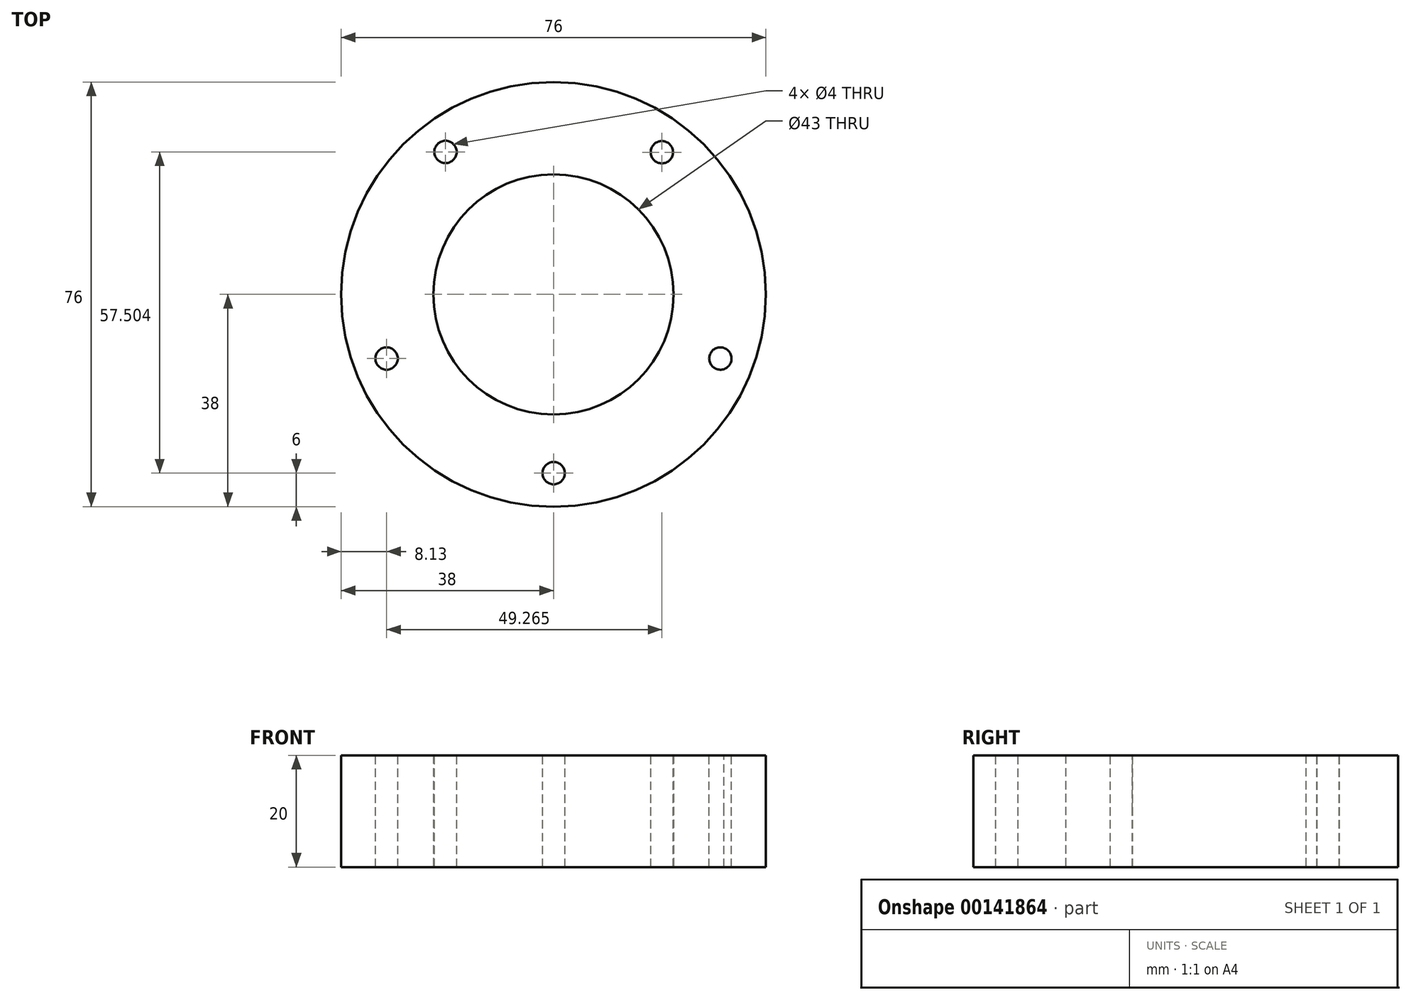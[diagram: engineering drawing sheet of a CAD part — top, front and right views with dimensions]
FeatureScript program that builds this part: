
annotation { "Feature Type Name" : "Feature", "Feature Type Description" : "" }
export const myFeature = defineFeature(function(context is Context, id is Id, definition is map)
    precondition{}
    {
        {
            var Q0;
            Q0=qCreatedBy(makeId("Top.planeOp"),FACE);
            var sketch = newSketch(context, id + "F0", { "sketchPlane" : qUnion([Q0])});
            skCircle(sketch, "E0", {"center": v(0, 0) * mm, "radius": 38 * mm});
            skCircle(sketch, "E1", {"center": v(0, 0) * mm, "radius": 21.5 * mm});
            skSolve(sketch);
        }
        {
            var Q0;
            Q0 = qSketchRegion(id + "F0", true);
            extrude(context, id + "F1", {"entities" : qUnion([Q0]), "depth" : 10 * mm});
        }
        {
            var Q0;
            Q0=makeQuery(id+"F1.opExtrude","CAP_FACE",FACE,{"disambiguationData":[OSD([sQuery(id+"F0.wireOp",EDGE,"E0"),sQuery(id+"F0.wireOp",EDGE,"E1")])],"isStart":false});
            var sketch = newSketch(context, id + "F2", { "sketchPlane" : qUnion([Q0])});
            skCircle(sketch, "E2", {"center": v(0, 0) * mm, "radius": 32 * mm});
            skCircle(sketch, "E3", {"center": v(-19.33, 25.5) * mm, "radius": 2 * mm});
            skCircle(sketch, "E4", {"center": v(19.4, 25.45) * mm, "radius": 2 * mm});
            skLineSegment(sketch, "E5", {"start": v(-17.33, 25.5) * mm, "end": v(17.4, 25.5) * mm});
            skLineSegment(sketch, "E6", {"start": v(0.03, 25.5) * mm, "end": v(0.03, -32) * mm});
            skCircle(sketch, "E7", {"center": v(0.03, -32) * mm, "radius": 2 * mm});
            skLineSegment(sketch, "E8", {"start": v(31.07, -7.66) * mm, "end": v(29.87, -11.48) * mm});
            skCircle(sketch, "E9", {"center": v(29.87, -11.48) * mm, "radius": 2 * mm});
            skLineSegment(sketch, "E10", {"start": v(29.87, -11.48) * mm, "end": v(-29.87, -11.48) * mm});
            skCircle(sketch, "E11", {"center": v(-29.87, -11.48) * mm, "radius": 2 * mm});
            skSolve(sketch);
        }
        {
            var Q0;
            {var subQ0=sQuery(id+"F2.wireOp",EDGE,"E3");var subQ1=sQuery(id+"F2.wireOp",EDGE,"E2");var subQ2=makeQuery(id+"F2.imprint","INTERSECT",VERTEX,{"disambiguationData":[OD(0.0)],"derivedFrom":[subQ1,subQ0]});Q0=makeQuery(id+"F2.imprint","IMPRINT",FACE,{"disambiguationData":[TD([[makeQuery(id+"F2.imprint","IMPRINT",EDGE,{"disambiguationData":[TD([[subQ2,-1.0]])],"derivedFrom":subQ1}),-1.0]])]});}
            var Q1;
            {var subQ0=sQuery(id+"F2.wireOp",EDGE,"E3");var subQ1=sQuery(id+"F2.wireOp",EDGE,"E2");var subQ2=makeQuery(id+"F2.imprint","INTERSECT",VERTEX,{"disambiguationData":[OD(0.0)],"derivedFrom":[subQ1,subQ0]});Q1=makeQuery(id+"F2.imprint","IMPRINT",FACE,{"disambiguationData":[TD([[makeQuery(id+"F2.imprint","IMPRINT",EDGE,{"disambiguationData":[TD([[subQ2,-1.0]])],"derivedFrom":subQ1}),1.0]])]});}
            var Q2;
            {var subQ0=sQuery(id+"F2.wireOp",EDGE,"E2");var subQ1=makeQuery(id+"F2.imprint","INTERSECT",VERTEX,{"derivedFrom":[subQ0,sQuery(id+"F2.wireOp",EDGE,"E10")]});Q2=makeQuery(id+"F2.imprint","IMPRINT",FACE,{"disambiguationData":[TD([[makeQuery(id+"F2.imprint","IMPRINT",EDGE,{"disambiguationData":[TD([[subQ1,1.0]])],"derivedFrom":subQ0}),-1.0]])]});}
            var Q3;
            {var subQ0=sQuery(id+"F2.wireOp",EDGE,"E10");var subQ1=sQuery(id+"F2.wireOp",EDGE,"E2");var subQ2=makeQuery(id+"F2.imprint","INTERSECT",VERTEX,{"derivedFrom":[subQ1,subQ0]});Q3=makeQuery(id+"F2.imprint","IMPRINT",FACE,{"disambiguationData":[TD([[makeQuery(id+"F2.imprint","IMPRINT",EDGE,{"disambiguationData":[TD([[subQ2,-1.0]])],"derivedFrom":subQ1}),1.0]])]});}
            var Q4;
            {var subQ0=sQuery(id+"F2.wireOp",EDGE,"E10");var subQ1=sQuery(id+"F2.wireOp",EDGE,"E2");var subQ2=makeQuery(id+"F2.imprint","INTERSECT",VERTEX,{"derivedFrom":[subQ1,subQ0]});Q4=makeQuery(id+"F2.imprint","IMPRINT",FACE,{"disambiguationData":[TD([[makeQuery(id+"F2.imprint","IMPRINT",EDGE,{"disambiguationData":[TD([[subQ2,1.0]])],"derivedFrom":subQ1}),1.0]])]});}
            var Q5;
            {var subQ0=sQuery(id+"F2.wireOp",EDGE,"E4");var subQ1=sQuery(id+"F2.wireOp",EDGE,"E2");var subQ2=makeQuery(id+"F2.imprint","INTERSECT",VERTEX,{"disambiguationData":[OD(0.0)],"derivedFrom":[subQ1,subQ0]});Q5=makeQuery(id+"F2.imprint","IMPRINT",FACE,{"disambiguationData":[TD([[makeQuery(id+"F2.imprint","IMPRINT",EDGE,{"disambiguationData":[TD([[subQ2,1.0]])],"derivedFrom":subQ1}),1.0]])]});}
            var Q6;
            {var subQ0=sQuery(id+"F2.wireOp",EDGE,"E4");var subQ1=sQuery(id+"F2.wireOp",EDGE,"E2");var subQ2=makeQuery(id+"F2.imprint","INTERSECT",VERTEX,{"disambiguationData":[OD(0.0)],"derivedFrom":[subQ1,subQ0]});Q6=makeQuery(id+"F2.imprint","IMPRINT",FACE,{"disambiguationData":[TD([[makeQuery(id+"F2.imprint","IMPRINT",EDGE,{"disambiguationData":[TD([[subQ2,1.0]])],"derivedFrom":subQ1}),-1.0]])]});}
            var Q7;
            {var subQ1=sQuery(id+"F2.wireOp",EDGE,"E2");var subQ3=sQuery(id+"F2.wireOp",EDGE,"E9");var subQ4=makeQuery(id+"F2.imprint","INTERSECT",VERTEX,{"disambiguationData":[OD(0.0)],"derivedFrom":[subQ1,subQ3]});Q7=makeQuery(id+"F2.imprint","IMPRINT",FACE,{"disambiguationData":[TD([[makeQuery(id+"F2.imprint","IMPRINT",EDGE,{"disambiguationData":[TD([[subQ4,1.0]])],"derivedFrom":subQ3}),1.0]])]});}
            var Q8;
            {var subQ0=sQuery(id+"F2.wireOp",EDGE,"E2");var subQ1=makeQuery(id+"F2.imprint","INTERSECT",VERTEX,{"derivedFrom":[subQ0,sQuery(id+"F2.wireOp",EDGE,"E6")]});Q8=makeQuery(id+"F2.imprint","IMPRINT",FACE,{"disambiguationData":[TD([[makeQuery(id+"F2.imprint","IMPRINT",EDGE,{"disambiguationData":[TD([[subQ1,1.0]])],"derivedFrom":subQ0}),-1.0]])]});}
            var Q9;
            {var subQ0=sQuery(id+"F2.wireOp",EDGE,"E6");var subQ1=sQuery(id+"F2.wireOp",EDGE,"E2");var subQ2=makeQuery(id+"F2.imprint","INTERSECT",VERTEX,{"derivedFrom":[subQ1,subQ0]});Q9=makeQuery(id+"F2.imprint","IMPRINT",FACE,{"disambiguationData":[TD([[makeQuery(id+"F2.imprint","IMPRINT",EDGE,{"disambiguationData":[TD([[subQ2,1.0]])],"derivedFrom":subQ1}),1.0]])]});}
            var Q10;
            {var subQ0=sQuery(id+"F2.wireOp",EDGE,"E6");var subQ1=sQuery(id+"F2.wireOp",EDGE,"E2");var subQ2=makeQuery(id+"F2.imprint","INTERSECT",VERTEX,{"derivedFrom":[subQ1,subQ0]});Q10=makeQuery(id+"F2.imprint","IMPRINT",FACE,{"disambiguationData":[TD([[makeQuery(id+"F2.imprint","IMPRINT",EDGE,{"disambiguationData":[TD([[subQ2,-1.0]])],"derivedFrom":subQ1}),1.0]])]});}
            var Q11;
            {var subQ0=sQuery(id+"F2.wireOp",EDGE,"E2");var subQ2=sQuery(id+"F2.wireOp",EDGE,"E9");var subQ3=makeQuery(id+"F2.imprint","INTERSECT",VERTEX,{"disambiguationData":[OD(0.0)],"derivedFrom":[subQ0,subQ2]});Q11=makeQuery(id+"F2.imprint","IMPRINT",FACE,{"disambiguationData":[TD([[makeQuery(id+"F2.imprint","IMPRINT",EDGE,{"disambiguationData":[TD([[subQ3,-1.0]])],"derivedFrom":subQ2}),1.0]])]});}
            var Q12;
            {var subQ1=sQuery(id+"F2.wireOp",EDGE,"E8");var subQ3=sQuery(id+"F2.wireOp",EDGE,"E9");var subQ4=makeQuery(id+"F2.imprint","INTERSECT",VERTEX,{"derivedFrom":[subQ1,subQ3]});Q12=makeQuery(id+"F2.imprint","IMPRINT",FACE,{"disambiguationData":[TD([[makeQuery(id+"F2.imprint","IMPRINT",EDGE,{"disambiguationData":[TD([[subQ4,-1.0]])],"derivedFrom":subQ3}),1.0]])]});}
            extrude(context, id + "F3", {"entities" : qUnion([Q0, Q1, Q2, Q3, Q4, Q5, Q6, Q7, Q8, Q9, Q10, Q11, Q12]), "operationType" : NewBodyOperationType.REMOVE, "oppositeDirection" : true, "depth" : 25 * mm});
        }
        {
            var Q0;
            Q0=makeQuery(id+"F3.boolean.opBoolean","COPY",FACE,{"derivedFrom":makeQuery(id+"F3.opExtrude","SWEPT_FACE",FACE,{"disambiguationData":[OSD([sQuery(id+"F2.wireOp",EDGE,"E8")])]})});
            extrude(context, id + "F4", {"entities" : qUnion([Q0]), "operationType" : NewBodyOperationType.REMOVE, "oppositeDirection" : true, "depth" : 0.1 * mm});
        }
        {
            var Q0;
            Q0=makeQuery(id+"F1.opExtrude","CAP_FACE",FACE,{"disambiguationData":[OSD([sQuery(id+"F0.wireOp",EDGE,"E0"),sQuery(id+"F0.wireOp",EDGE,"E1")])],"isStart":false});
            extrude(context, id + "F5", {"entities" : qUnion([Q0]), "operationType" : NewBodyOperationType.ADD, "depth" : 10 * mm});
        }
    });
